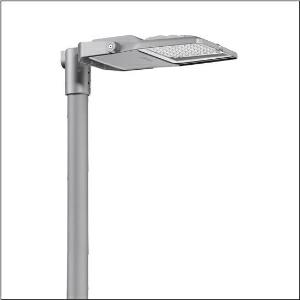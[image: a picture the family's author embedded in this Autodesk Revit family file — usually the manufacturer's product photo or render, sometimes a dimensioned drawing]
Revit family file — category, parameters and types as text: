
# Revit family: floodlight_fl_21_iq_mini___pl61_5xa7772b2c3a_0206
name_source: partatom
category: Lighting Fixtures
units: mm (PartAtom-declared; Revit-internal decimal feet)

## family parameters
Cut with Voids When Loaded = No
Host = Face
Light Source = No
Part Type = Normal
Room Calculation Point = No
Round Connector Dimension = Use Diameter
Shared = No

## types (1)
- --- (1 x LED, 6120 lm, 45.5 W, 3000K)
    Apparent Load = 46 VA
    CIE Flux Codes = 33 65 98 100 100
    Color Rendering = 70
    Color Temperature = 3000K
    Default Elevation = 1800 mm
    Description = Floodlight FL 21 iQ mini, floodlight, primary light control with lens, of PMMA, primary optical cover: protective disc, of toughened safety glass, transparent, light distribution: PL61, light emission: direct distribution, installation type: surface-mounted, LED, High Power LED, rated luminous flux: 6.120lm, luminous efficacy: 135lm/W, light colour: 730, colour temperature: 3000K, control: Auto-Match, Temp-Guard, Night-Set, Smart-Wire, Desk-Remote (wireless, voltage-free reading and setting of iQ features in the workshop via application-optimized NFC function/RFID function), optimised constant luminous flux control (CLO 2.0), Light-Fading, Lumen-Switch, with terminal, 6-pole, mains connection: 220..240V, AC, 50/60Hz, start of lifetime: 46W, end of service life: 48W, reduction: 22W, luminaire housing, of diecast aluminium, powder-coated, Siteco® metallic grey (DB 702S), corrosivity category C5 mid according to DIN EN ISO 12944, sealing non-destructively replaceable, please order mast flange separately, mast bracket, of steel, galvanised, powder-coated, protection rating (complete): IP66, insulation class (complete): insulation class II (safety insulation), certification: CE, ENEC, VDE, protection symbol: D, impact resistance: IK08, permissible operating ambient temperature: -40..+40°C, permissible operating ambient temperature for outdoor applications: -40..+50°C, standard: DIN EN 12944, LABS conformity tested according to VDMA 24364:2018-05, packaging unit: 1 piece

Light Distribution: PL61
    Height = 70 mm
    Lamp = 1 x LED
    Lamp Light Flux = 6120 lm
    Lamp Power = 45.5 W
    Lamp count = 1
    Length = 485 mm
    Luminous efficacy = 135 lm/W
    Manufacturer = Siteco
    ModVariant = No
    Model = 5XA7772B2C3A
    Number of Poles = 1
    OnlyDefault = Yes
    Power Factor = 1
    Product Name = Floodlight FL 21 iQ mini | PL61
    Product group = floodlight | pylon annexe
    ProductGroupID = 6200
    Protection Class = Protection class II
    Protection Degree = IP 66
    RLX_Detail_Level = 1
    RLX_Emergency_Light_Flux = 0 lm
    RLX_Emergency_Type = 0
    RLX_Emergency_Type_DB = No
    RlxData = <blob elided: 101149 chars, md5=82912ed9>
    Socket = socket
    Standby Power = 0 W
    System Light Flux = 6120 lm
    System Power = 46 W
    Type Comments = factory setting: luminous flux: 100 % | dim-lin: 254 | 463 mA
    Type Image = l_1007125.jpg
    URL = http://relux.com
    VarID = @adj_106659
    Voltage = 0 V
    Weight = 0.00 kg
    Width = 337 mm

## geometry (parser evidence)
native form markers: Blend x4, Sweep x12
no freeform markers — native parametric forms only
